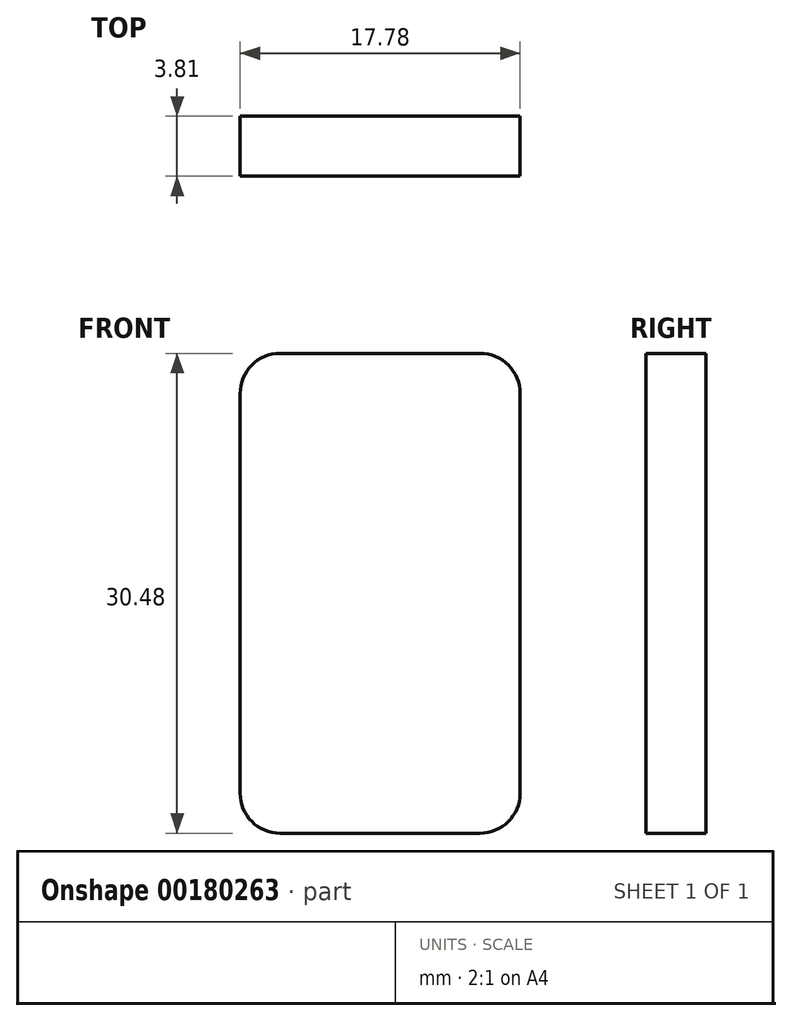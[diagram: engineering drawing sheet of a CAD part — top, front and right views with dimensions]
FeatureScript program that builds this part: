
annotation { "Feature Type Name" : "Feature", "Feature Type Description" : "" }
export const myFeature = defineFeature(function(context is Context, id is Id, definition is map)
    precondition{}
    {
        {
            var Q0;
            Q0=qCreatedBy(makeId("Front.planeOp"),FACE);
            var sketch = newSketch(context, id + "F0", { "sketchPlane" : qUnion([Q0])});
            skLineSegment(sketch, "E0.bottom", {"start": v(-26.87, 9.47) * mm, "end": v(-9.1, 9.47) * mm});
            skLineSegment(sketch, "E0.top", {"start": v(-26.87, -21.01) * mm, "end": v(-9.1, -21.01) * mm});
            skLineSegment(sketch, "E0.left", {"start": v(-26.87, 9.47) * mm, "end": v(-26.87, -21.01) * mm});
            skLineSegment(sketch, "E0.right", {"start": v(-9.1, 9.47) * mm, "end": v(-9.1, -21.01) * mm});
            skSolve(sketch);
        }
        {
            var Q0;
            Q0 = qSketchRegion(id + "F0", true);
            extrude(context, id + "F1", {"entities" : qUnion([Q0]), "depth" : 3.8 * mm});
        }
        {
            var Q0;
            Q0=makeQuery(id+"F1.opExtrude","SWEPT_EDGE",EDGE,{"disambiguationData":[OSD([sQuery(id+"F0.wireOp",EDGE,"E0.bottom"),sQuery(id+"F0.wireOp",EDGE,"E0.right")])]});
            var Q1;
            Q1=makeQuery(id+"F1.opExtrude","SWEPT_EDGE",EDGE,{"disambiguationData":[OSD([sQuery(id+"F0.wireOp",EDGE,"E0.bottom"),sQuery(id+"F0.wireOp",EDGE,"E0.left")])]});
            fillet(context, id + "F2", {"entities" : qUnion([Q0, Q1]), "radius" : 2.54 * mm, "tangentPropagation" : true, "allowEdgeOverflow" : false});
        }
        {
            var Q0;
            Q0=makeQuery(id+"F1.opExtrude","SWEPT_EDGE",EDGE,{"disambiguationData":[OSD([sQuery(id+"F0.wireOp",EDGE,"E0.top"),sQuery(id+"F0.wireOp",EDGE,"E0.left")])]});
            var Q1;
            Q1=makeQuery(id+"F1.opExtrude","SWEPT_EDGE",EDGE,{"disambiguationData":[OSD([sQuery(id+"F0.wireOp",EDGE,"E0.top"),sQuery(id+"F0.wireOp",EDGE,"E0.right")])]});
            fillet(context, id + "F3", {"entities" : qUnion([Q0, Q1]), "radius" : 2.54 * mm, "tangentPropagation" : true, "allowEdgeOverflow" : false});
        }
    });
